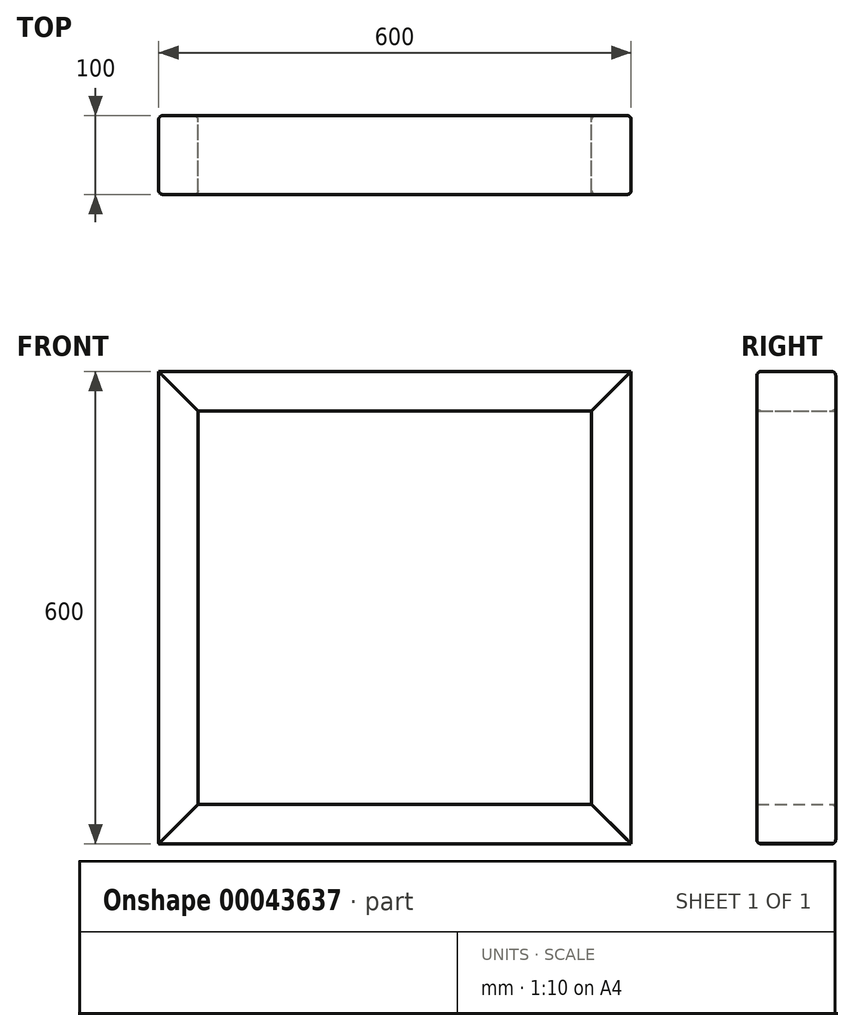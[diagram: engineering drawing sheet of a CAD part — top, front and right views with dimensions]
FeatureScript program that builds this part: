
annotation { "Feature Type Name" : "Feature", "Feature Type Description" : "" }
export const myFeature = defineFeature(function(context is Context, id is Id, definition is map)
    precondition{}
    {
        {
            var Q0;
            Q0=qCreatedBy(makeId("Front.planeOp"),FACE);
            var sketch = newSketch(context, id + "F6", { "sketchPlane" : qUnion([Q0])});
            skLineSegment(sketch, "E0.bottom", {"start": v(-585.12, -600) * mm, "end": v(-1185.12, -600) * mm});
            skLineSegment(sketch, "E0.top", {"start": v(-585.12, 0) * mm, "end": v(-1185.12, 0) * mm});
            skLineSegment(sketch, "E0.left", {"start": v(-585.12, -600) * mm, "end": v(-585.12, 0) * mm});
            skLineSegment(sketch, "E0.right", {"start": v(-1185.12, -600) * mm, "end": v(-1185.12, 0) * mm});
            skLineSegment(sketch, "E1.0", {"start": v(-635.12, -50) * mm, "end": v(-1135.12, -50) * mm});
            skLineSegment(sketch, "E2.0", {"start": v(-1135.12, -600) * mm, "end": v(-1135.12, -599.75) * mm});
            skLineSegment(sketch, "E3.0", {"start": v(-635.12, -550) * mm, "end": v(-1135.12, -550) * mm});
            skLineSegment(sketch, "E4.trimOffspring", {"start": v(-635.12, -550) * mm, "end": v(-635.12, -50) * mm});
            skLineSegment(sketch, "E5", {"start": v(-1185.12, -600) * mm, "end": v(-1135.12, -550) * mm});
            skLineSegment(sketch, "E6", {"start": v(-1135.12, -50) * mm, "end": v(-1185.12, 0) * mm});
            skLineSegment(sketch, "E7", {"start": v(-635.12, -50) * mm, "end": v(-585.12, 0) * mm});
            skLineSegment(sketch, "E8", {"start": v(-585.12, -599.75) * mm, "end": v(-635.12, -550) * mm});
            skLineSegment(sketch, "E9.trimOffspring", {"start": v(-1135.12, -550) * mm, "end": v(-1135.12, -50) * mm});
            skLineSegment(sketch, "E10.trimOffspring", {"start": v(-1184.87, -599.75) * mm, "end": v(-1185.12, -599.75) * mm});
            skSolve(sketch);
        }
        {
            var Q0;
            Q0=makeQuery(id+"F6.imprint","IMPRINT",FACE,{"disambiguationData":[TD([[makeQuery(id+"F6.imprint","IMPRINT",EDGE,{"derivedFrom":sQuery(id+"F6.wireOp",EDGE,"E0.top")}),1.0]])]});
            extrude(context, id + "F0", {"entities" : qUnion([Q0]), "depth" : 100 * mm});
        }
        {
            var Q0;
            {var subQ1=sQuery(id+"F6.wireOp",EDGE,"E6");Q0=makeQuery(id+"F6.imprint","IMPRINT",FACE,{"disambiguationData":[TD([[makeQuery(id+"F6.imprint","IMPRINT",EDGE,{"derivedFrom":subQ1}),1.0]])]});}
            extrude(context, id + "F7", {"entities" : qUnion([Q0]), "depth" : 100 * mm});
        }
        {
            var Q0;
            {var subQ1=sQuery(id+"F6.wireOp",EDGE,"E3.0");Q0=makeQuery(id+"F6.imprint","IMPRINT",FACE,{"disambiguationData":[TD([[makeQuery(id+"F6.imprint","IMPRINT",EDGE,{"derivedFrom":subQ1}),1.0]])]});}
            extrude(context, id + "F1", {"entities" : qUnion([Q0]), "depth" : 100 * mm});
        }
        {
            var Q0;
            Q0=makeQuery(id+"F6.imprint","IMPRINT",FACE,{"disambiguationData":[TD([[makeQuery(id+"F6.imprint","IMPRINT",EDGE,{"derivedFrom":sQuery(id+"F6.wireOp",EDGE,"E4.trimOffspring")}),-1.0]])]});
            extrude(context, id + "F2", {"entities" : qUnion([Q0]), "depth" : 100 * mm});
        }
        {
            var Q0;
            Q0=makeQuery(id+"F0.opExtrude","CAP_EDGE",EDGE,{"disambiguationData":[OSD([sQuery(id+"F6.wireOp",EDGE,"E0.top")])],"isStart":false});
            var Q1;
            Q1=makeQuery(id+"F0.opExtrude","CAP_EDGE",EDGE,{"disambiguationData":[OSD([sQuery(id+"F6.wireOp",EDGE,"E1.0")])],"isStart":false});
            var Q2;
            Q2=makeQuery(id+"F7.opExtrude","CAP_EDGE",EDGE,{"disambiguationData":[OSD([sQuery(id+"F6.wireOp",EDGE,"E0.right")])],"isStart":false});
            var Q3;
            Q3=makeQuery(id+"F1.opExtrude","CAP_EDGE",EDGE,{"disambiguationData":[OSD([sQuery(id+"F6.wireOp",EDGE,"222565d4-c493-4b6c-8dfb-7e01182643c8.0")])],"isStart":false});
            var Q4;
            Q4=makeQuery(id+"F2.opExtrude","CAP_EDGE",EDGE,{"disambiguationData":[OSD([sQuery(id+"F6.wireOp",EDGE,"E0.left")])],"isStart":false});
            fillet(context, id + "F3", {"entities" : qUnion([Q0, Q1, Q2, Q3, Q4]), "radius" : 5 * mm, "tangentPropagation" : true, "allowEdgeOverflow" : false});
        }
        {
            var Q0;
            Q0=makeQuery(id+"F1.opExtrude","CAP_EDGE",EDGE,{"disambiguationData":[OSD([sQuery(id+"F6.wireOp",EDGE,"E0.bottom")])],"isStart":false});
            fillet(context, id + "F4", {"entities" : qUnion([Q0]), "radius" : 5 * mm, "tangentPropagation" : true, "allowEdgeOverflow" : false});
        }
        {
            var Q0;
            Q0=makeQuery(id+"F1.opExtrude","CAP_EDGE",EDGE,{"disambiguationData":[OSD([sQuery(id+"F6.wireOp",EDGE,"E0.bottom")])],"isStart":true});
            fillet(context, id + "F8", {"entities" : qUnion([Q0]), "radius" : 5 * mm, "tangentPropagation" : true, "allowEdgeOverflow" : false});
        }
        {
            var Q0;
            Q0=makeQuery(id+"F2.opExtrude","CAP_EDGE",EDGE,{"disambiguationData":[OSD([sQuery(id+"F6.wireOp",EDGE,"E0.left")])],"isStart":true});
            var Q1;
            Q1=makeQuery(id+"F0.opExtrude","CAP_EDGE",EDGE,{"disambiguationData":[OSD([sQuery(id+"F6.wireOp",EDGE,"E1.0")])],"isStart":true});
            var Q2;
            Q2=makeQuery(id+"F0.opExtrude","CAP_EDGE",EDGE,{"disambiguationData":[OSD([sQuery(id+"F6.wireOp",EDGE,"E0.top")])],"isStart":true});
            var Q3;
            Q3=makeQuery(id+"F7.opExtrude","CAP_EDGE",EDGE,{"disambiguationData":[OSD([sQuery(id+"F6.wireOp",EDGE,"E0.right")])],"isStart":true});
            var Q4;
            Q4=makeQuery(id+"F7.opExtrude","CAP_EDGE",EDGE,{"disambiguationData":[OSD([sQuery(id+"F6.wireOp",EDGE,"E9.trimOffspring")])],"isStart":true});
            var Q5;
            Q5=makeQuery(id+"F1.opExtrude","CAP_EDGE",EDGE,{"disambiguationData":[OSD([sQuery(id+"F6.wireOp",EDGE,"E3.0")])],"isStart":true});
            fillet(context, id + "F5", {"entities" : qUnion([Q0, Q1, Q2, Q3, Q4, Q5]), "radius" : 5 * mm, "tangentPropagation" : true, "allowEdgeOverflow" : false});
        }
    });
